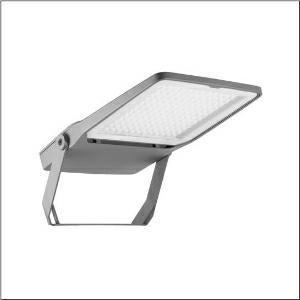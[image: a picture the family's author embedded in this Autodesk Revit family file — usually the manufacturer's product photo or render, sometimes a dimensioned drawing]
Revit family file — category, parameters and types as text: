
# Revit family: floodlight_fl_20_midi___pl61_5xa7681d2c1ac_c278
name_source: partatom
category: Lighting Fixtures
units: mm (PartAtom-declared; Revit-internal decimal feet)

## family parameters
Cut with Voids When Loaded = No
Host = Face
Light Source = No
Part Type = Normal
Room Calculation Point = No
Round Connector Dimension = Use Diameter
Shared = No

## types (1)
- Floodlight FL 20 midi  PL61 (1 x LED 4000K / CRI = 70 (unbekannt), 18200 lm, 4000K)
    Apparent Load = 142 VA
    CIE Flux Codes = 33 65 98 100 100
    Color Rendering = 70
    Color Temperature = 4000K
    Default Elevation = 1800 mm
    Description = Floodlight FL 20 midi, floodlight, primary light control with lens, of plastic, primary optical cover: protective disc, of toughened safety glass, transparent, light distribution: PL61, light emission: direct distribution, primary light characteristic: asymmetric, installation type: surface-mounted, LED High Power LED, rated luminous flux: 18.200 lm, light colour: 740, colour temperature: 4000K, control gear: ECG Basic, control: power reduction, overheat protection, electronic power reduction, with terminal, 5-pole, max. 2.5mm², mains connection: 220..240V, AC, 50/60Hz, rated input power: 142W, LED unit, of diecast aluminium, powder-coated, Siteco® metallic grey (DB 702S), length: 654 mm, width: 450 mm, height: 76mm, housing frame, of diecast aluminium, powder-coated, Siteco® metallic grey (DB 702S), mounting bracket, of steel, powder-coated, Siteco® metallic grey (DB 702S), ON/OFFprotection rating (complete): IP66, insulation class (complete): insulation class I (protective earthing), certification: CE, ENEC, VDE, protection symbol: D, permissible ambient temperature for indoor applications: -40..+40°C, permissible ambient temperature for outdoor applications: -40..+50°C, standard: DIN EN 12944, packaging unit: 1 piece

Light Distribution: PL61
    Height = 76 mm
    Lamp = 1 x LED 4000K / CRI >= 70 (unbekannt)
    Lamp Light Flux = 18200 lm
    Lamp count = 1
    Length = 672 mm
    Luminous efficacy = 128 lm/W
    Manufacturer = Siteco
    ModVariant = No
    Model = 5XA7681D2C1AC
    Number of Poles = 1
    OnlyDefault = Yes
    Power Factor = 1
    Product Name = Floodlight FL 20 midi | PL61
    Product group = floodlight | pylon top
    ProductGroupID = 6101
    Protection Class = Protection class I
    Protection Degree = IP 66
    RLX_Detail_Level = 1
    RlxData = <blob elided: 94061 chars, md5=4f07dff9>
    Socket = socket
    Standby Power = 0 W
    System Light Flux = 18200 lm
    System Power = 142 W
    Type Comments = Product without accessories
    Type Image = l_1005943.jpg
    URL = http://relux.com
    VarID = ---
    Voltage = 0 V
    Weight = 0.00 kg
    Width = 450 mm

## geometry (parser evidence)
native form markers: Blend x4, Sweep x14
no freeform markers — native parametric forms only
